# Revit family: NBS_Allermuir_DmstcChrs_Mote-en-us_Ottoman
name_source: partatom
category: Furniture
revit_build: Autodesk Revit 2016 (Build: 20151007_0715(x64)
units: mm (PartAtom-declared; Revit-internal decimal feet)

## family parameters
Always vertical = Yes
Cut with Voids When Loaded = No
Room Calculation Point = No
Shared = No
Work Plane-Based = No

## types (3) — shared parameters
AssetType = Moveable
Category = Pr_40_50_12_22:Dining chairs
Depth = 29 "
DurationUnit = year
ExpectedLife = 10
FrameColourOptions = Flint grey, mineral sand, mellow yellow, orange crush
FrameHeight = 10 "
FrameMountingMaterial = NBS_Concept
FramesColour = Black
FramesFinish = Powder coat
FramesMaterial = Aluminium
IfcExportAs = IfcFurnitureType
IfcExportType = SOFA
IsBuiltIn = No
ManufacturerName = Allermuir
ManufacturerURL = http://www.thesenatorgroup.com
ModelReference = Mote ottoman
NBSCertification = www.nationalbimlibrary.com/cert/pvl4jefk
NBSDescription = Domestic chairs
NBSReference = 45-35-20/365
NominalHeight = 19 "
NominalLength = 29 "
OmniClassCode = 22-12 52 23
OmniClassTitle = Office Seating
OmniClassVersion = Table 22 2012-05-16
ProductInformation = http://www.thesenatorgroup.com
SeatArmRestHeight = 24 "
SeatEndRestOffset = 3 "
SeatFrameMaterial = NBS_Concept
SeatFrameWidth = 2 "
SeatLegOffset = 6 "
SeatPowerSupplyMaterial = NBS_Concept
SeatingArmRestMaterial = NBS_Concept
SeatingHeight = 19 "
SeatingSeatMaterial = NBS_Concept
SeatsAndBacksFinish = Two-tone upholstery available
SeatsAndBacksMaterial = Upholstered
SingleSeatWidth = 39 "
Status = UNSET
ThreeSeatWidth = 87 "
TwoSeatWidth = 63 "
Uniclass2015Code = Pr_40_50_12_22
Uniclass2015Title = Dining chairs
Uniclass2015Version = Products v1.9
Version = 1
WarrantyDescription = Allermuir warrant that its manufactured products are free from manufacturing defects in materials or workmanship for a period of ten years
WarrantyDurationParts = 10
WarrantyDurationUnit = year
zero-valued in all types: HighestSeatingHeight, LowestSeatingHeight

## per-type parameters (varying)
| type | BIMObjectName | Description | Features | IsSingleSeat | IsThreeSeat | IsTwoSeat | LeftSeatPositionOffset | ModelNumber | Name | NominalDepth | NominalWidth | OptionalAccessories | RightSeatPositionWidth | SeatOverallWidth | ShowMultipleSeat | Size |
| MTEOT01 | NBS_Allermuir_DomesticChairs_Mote_MTEOT01-US | Single seat ottoman | Fully upholstered, cast aluminum legs and aluminum perimeter frame finished in black powder coat, plastic glides with leveling adjustment, Cast aluminum frame available in flint gray, mineral sand, mellow yellow or orange crush, 1 x front facing, frame integrated power unit - 2 x powered USB and 1 x power outlet, 1 x rear facing, frame integrated power unit, 2 x powered USB and 1 x power outlet | Yes | No | No | 0 " | MTE-OT01 | DomesticChairs_Mote_MTE-OT01_Allermuir | 39 " | 39 " | 1 x front facing frame intergrated power unit with 2 x powered USB and 1 x power socket, 1 x rear facing frame intergrated power unit with 2 x powered USB and 1 x power socket | 16 " | 39 " | No | 28.75 x 39.25 x 18.5" |
| MTEOT02 | NBS_Allermuir_DomesticChairs_Mote_MTEOT02-US | Two seat ottoman | Fully upholstered, cast aluminum legs and aluminum perimeter frame finished in black powder coat, plastic glides with leveling adjustment, cast aluminum frame available in flint gray, mineral sand, mellow yellow or orange crush, 1 x front facing, frame integrated power unit - 2 x powered USB and 1 x power outlet, 1 x Rear facing, frame integrated power unit - 2 x powered USB and 1 x power outlet, end arms, single arm - mid | No | No | Yes | 0 " | MTE-OT02 | DomesticChairs_Mote_MTE-OT02_Allermuir | 63 " | 63 " | 1 x front facing frame intergrated power unit with 2 x powered USB and 1 x power socket, 1 x rear facing, frame intergrated power unit with 2 x powered USB and 1 x power socket, End arms, Single arm - mid | 16 " | 63 " | Yes | 28.75 x 63 x 18.5" |
| MTEOT03 | NBS_Allermuir_DomesticChairs_Mote_MTEOT03-US | Three seat ottoman | Fully upholstered, cast aluminium legs and aluminium perimeter frame finished in black powder coat, plastic glides with leveling adjustment, cast aluminum frame available in flint gray, mineral sand, mellow yellow or orange crush, 2 x front facing, frame integrated power unit - 2 x powered USB and 1 x power outlet, 2 x rear facing, frame integrated power unit - 2 x powered USB and 1 x power outlet, two-tone upholstery, end arms, double arms - intermediated | No | Yes | No | 16 " | MTE-OT03 | DomesticChairs_Mote_MTE-OT03_Allermuir | 87 " | 87 " | 2 x front facing frame intergrated power unit with 2 x powered USB and 1 x power socket, 2 x rear facing, frame intergrated power unit with 2 x powered USB and 1 x power socket, end arms, double arms - intermediated | 31 " | 87 " | Yes | 28.75 x 86.5 x 18.5" |

## geometry (parser evidence)
native form markers: Sweep x12
no freeform markers — native parametric forms only
